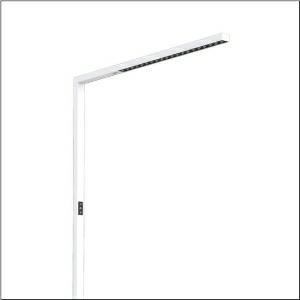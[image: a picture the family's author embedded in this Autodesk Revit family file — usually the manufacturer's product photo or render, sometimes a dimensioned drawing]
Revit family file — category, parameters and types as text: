
# Revit family: silica_r__31_floor_51my52fa4cw_1f6d
name_source: partatom
category: Lighting Fixtures
units: mm (PartAtom-declared; Revit-internal decimal feet)

## family parameters
Cut with Voids When Loaded = No
Host = Face
Light Source = No
Part Type = Normal
Room Calculation Point = No
Round Connector Dimension = Use Diameter
Shared = No

## types (1)
- Silica® 31 Floor (1 x LED, 10600 lm, 75 W, 4000K)
    Apparent Load = 75 VA
    CIE Flux Codes = 86 100 100 24 100
    Color Rendering = 80
    Color Temperature = 4000K
    Default Elevation = 1800 mm
    Description = Silica® 31 Floor, floorstanding luminaire, secondary optical cover: cover panel, of PMMA, light emission: direct/indirect distribution, primary light characteristic: symmetric, installation type: not mounted, LED, rated luminous flux: 10.600lm, luminous efficacy: 141lm/W, light colour: 840, colour temperature: 4000K, control gear: Touchdim, daylight-dependent control, with cable with plug, mains connection: 230V, AC, 50Hz, connection cable pre-assembled, rated input power: 75W, luminaire head, of aluminium, traffic white (RAL 9016), length: 1.203mm, width: 52mm, supporting column, angular, of aluminium, traffic white (RAL 9016), baseplate, of steel, traffic white (RAL 9016), protection rating (complete): IP20, insulation class (complete): insulation class I (protective earthing), certification: CE, permissible operating ambient temperature: -20..+40°C, standard: EN 50419, packaging unit: 1 piece
    Height = 36 mm
    Lamp = 1 x LED
    Lamp Light Flux = 10600 lm
    Lamp Power = 75 W
    Lamp count = 1
    Length = 1203 mm
    Luminous efficacy = 141 lm/W
    Manufacturer = Siteco
    ModVariant = No
    Model = 51MY52FA4CW
    Mounting Place = Floor
    Mounting Type = Freestanding
    Number of Poles = 1
    OnlyDefault = Yes
    Power Factor = 1
    Product Name = Silica® 31 Floor
    Product group = floorstanding luminaire
    ProductGroupID = 1302
    Protection Class = Protection class I
    Protection Degree = IP 20
    RLX_Detail_Level = 1
    RLX_Emergency_Light_Flux = 0 lm
    RLX_Emergency_Type = 0
    RLX_Emergency_Type_DB = No
    RlxData = <blob elided: 17149 chars, md5=4ded2531>
    Socket = socket
    Standby Power = 0 W
    System Light Flux = 10600 lm
    System Power = 75 W
    Type Comments = Product without accessories
    Type Image = l_1275309.jpg
    URL = http://relux.com
    VarID = ---
    Voltage = 0 V
    Weight = 0.00 kg
    Width = 52 mm  [stored 0.170604 ft]

note: [stored X ft] marks values corroborated as IEEE doubles in the binary element streams (Revit-internal decimal feet)

## geometry (parser evidence)
native form markers: Blend x4, Sweep x16
no freeform markers — native parametric forms only
